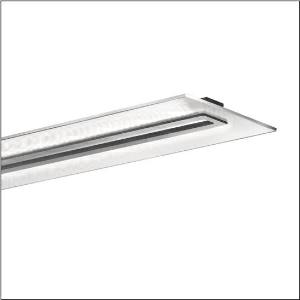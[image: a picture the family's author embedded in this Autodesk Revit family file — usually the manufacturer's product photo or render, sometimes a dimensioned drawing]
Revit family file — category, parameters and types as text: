
# Revit family: vega_r__11_5mn238dle003_bbe2
name_source: partatom
category: Lighting Fixtures
units: mm (PartAtom-declared; Revit-internal decimal feet)

## family parameters
Cut with Voids When Loaded = No
Host = Face
Light Source = No
Part Type = Normal
Room Calculation Point = No
Round Connector Dimension = Use Diameter
Shared = No

## types (1)
- --- (1 x LED 3000K / CRI = 80 (unbekannt), 7300 lm, 3000K)
    Apparent Load = 62 VA
    CIE Flux Codes = 61 86 97 62 100
    Color Rendering = 80
    Color Temperature = 3000K
    Default Elevation = 1800 mm
    Description = Vega® 11, office luminaire, primary light control with prismatic reflector, of PMMA, transparent prismatic structure, CAT 2 (L<= 1500cd/m²), light emission: direct/indirect distribution, primary light characteristic: symmetric, installation type: suspended mounting, surface-mounted, LED, rated luminous flux: 7.300lm, luminous efficacy: 118lm/W, light colour: 830, colour temperature: 3000K, control gear: ECG, with terminal, 3+2-pole, max. 2.5mm², mains connection: 230V, AC, 50Hz, connection cable inclusive, cable length: 1,5m, rated input power: 62W, luminaire housing, rectangular, rounded, of aluminium section, anodised, metallic grey (RAL 9006), length: 1.250mm, width: 350mm, height: 43mm, luminaire housing, lower part, of aluminium section, anodised, metallic grey (RAL 9006), of PC, grey, protection rating (complete): IP20, insulation class (complete): insulation class I (protective earthing), certification: CE, standard: EN 50419, packaging unit: 1 piece
    Height = 40 mm  [stored 0.131234 ft]
    Lamp = 1 x LED 3000K / CRI >= 80 (unbekannt)
    Lamp Light Flux = 7300 lm
    Lamp count = 1
    Length = 1250 mm
    Luminous efficacy = 118 lm/W
    Manufacturer = Siteco
    ModVariant = No
    Model = 5MN238DLE003
    Mounting Place = Ceiling
    Mounting Type = Pendant
    Number of Poles = 1
    OnlyDefault = Yes
    Power Factor = 1
    Product Name = Vega® 11
    Product group = office luminaire | ceiling pendant
    ProductGroupID = 902
    Protection Class = Protection class I
    Protection Degree = IP 20
    RLX_Detail_Level = 1
    RLX_Emergency_Light_Flux = 0 lm
    RLX_Emergency_Type = 0
    RLX_Emergency_Type_DB = No
    RlxData = <blob elided: 62645 chars, md5=eb5dfc10>
    Socket = socket
    Standby Power = 0 W
    System Light Flux = 7300 lm
    System Power = 62 W
    Type Comments = factory setting: luminous flux: 100 % | dim-lin: 254 | 460 mA
    Type Image = l_1004807.jpg
    URL = http://relux.com
    VarID = @adj_149797
    Voltage = 0 V
    Weight = 0.00 kg
    Width = 350 mm

note: [stored X ft] marks values corroborated as IEEE doubles in the binary element streams (Revit-internal decimal feet)

## geometry (parser evidence)
native form markers: Blend x4, Sweep x10
no freeform markers — native parametric forms only
